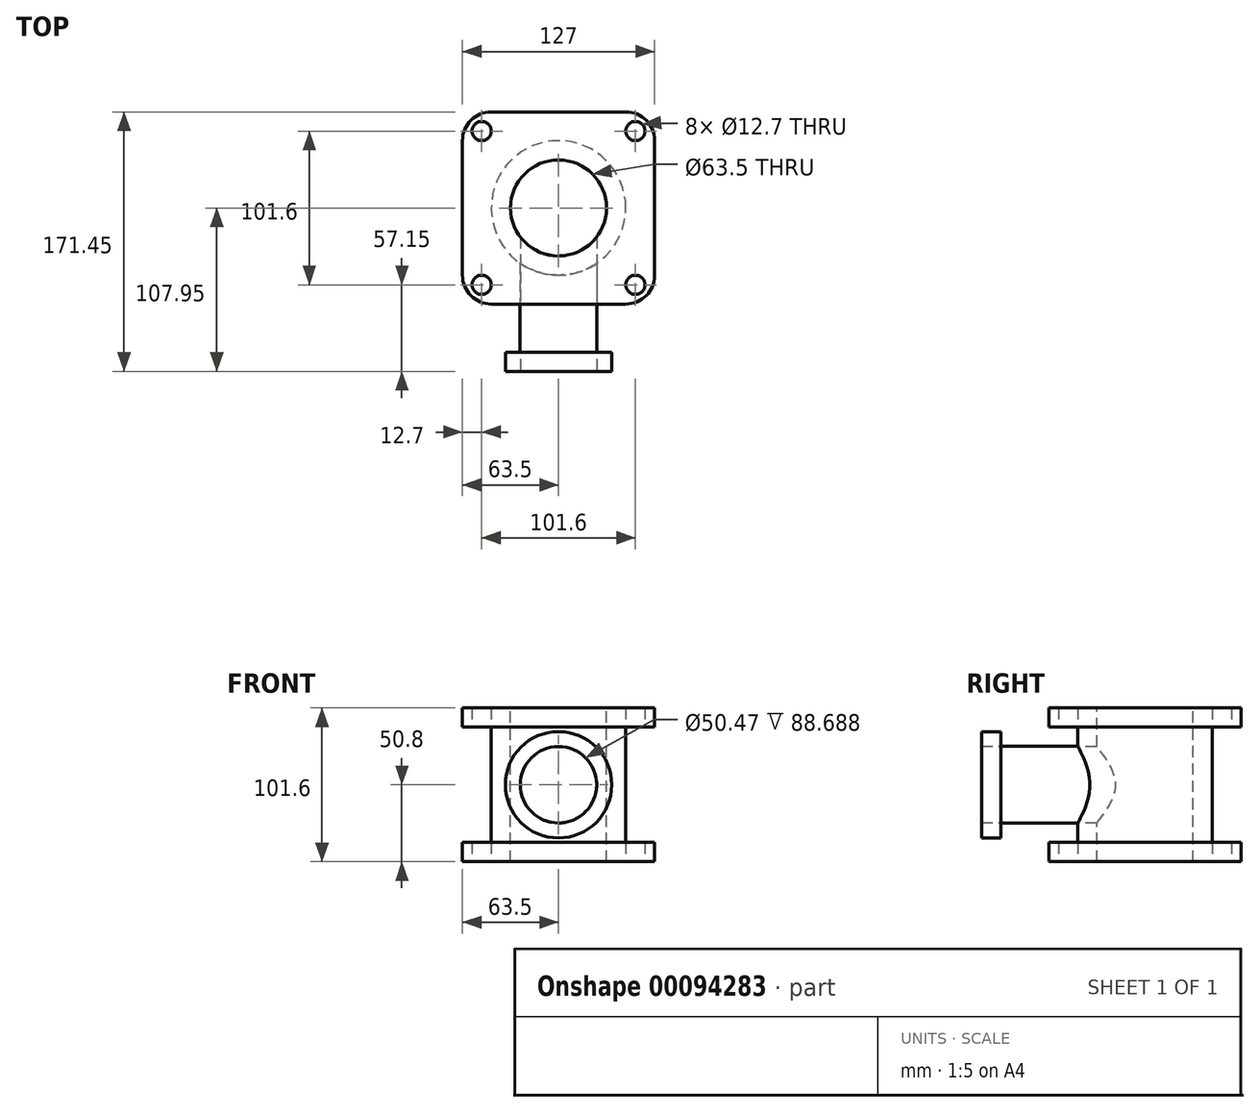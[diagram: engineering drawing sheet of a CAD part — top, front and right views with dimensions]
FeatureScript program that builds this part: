
annotation { "Feature Type Name" : "Feature", "Feature Type Description" : "" }
export const myFeature = defineFeature(function(context is Context, id is Id, definition is map)
    precondition{}
    {
        {
            var Q0;
            Q0=qCreatedBy(makeId("Top.planeOp"),FACE);
            var sketch = newSketch(context, id + "F0", { "sketchPlane" : qUnion([Q0])});
            skLineSegment(sketch, "E0.bottom", {"start": v(63.5, 63.5) * mm, "end": v(-63.5, 63.5) * mm});
            skLineSegment(sketch, "E0.top", {"start": v(63.5, -63.5) * mm, "end": v(-63.5, -63.5) * mm});
            skLineSegment(sketch, "E0.left", {"start": v(63.5, 63.5) * mm, "end": v(63.5, -63.5) * mm});
            skLineSegment(sketch, "E0.right", {"start": v(-63.5, 63.5) * mm, "end": v(-63.5, -63.5) * mm});
            skPoint(sketch, "E0.middle", {"position": v(0, 0) * mm});
            skCircle(sketch, "E1", {"center": v(-50.8, -50.8) * mm, "radius": 6.35 * mm});
            skCircle(sketch, "E2.MirrorC", {"center": v(-50.8, 50.8) * mm, "radius": 6.35 * mm});
            skCircle(sketch, "E3.MirrorC", {"center": v(50.8, 50.8) * mm, "radius": 6.35 * mm});
            skCircle(sketch, "E4.MirrorC", {"center": v(50.8, -50.8) * mm, "radius": 6.35 * mm});
            skSolve(sketch);
        }
        {
            var Q0;
            Q0=makeQuery(id+"F0.imprint","IMPRINT",FACE,{"disambiguationData":[TD([[makeQuery(id+"F0.imprint","IMPRINT",EDGE,{"derivedFrom":sQuery(id+"F0.wireOp",EDGE,"E0.bottom")}),1.0]])]});
            extrude(context, id + "F1", {"entities" : qUnion([Q0]), "depth" : 12.7 * mm});
        }
        {
            var Q0;
            Q0=makeQuery(id+"F1.opExtrude","SWEPT_EDGE",EDGE,{"disambiguationData":[OSD([sQuery(id+"F0.wireOp",EDGE,"E0.bottom"),sQuery(id+"F0.wireOp",EDGE,"E0.right")])]});
            var Q1;
            Q1=makeQuery(id+"F1.opExtrude","SWEPT_EDGE",EDGE,{"disambiguationData":[OSD([sQuery(id+"F0.wireOp",EDGE,"E0.top"),sQuery(id+"F0.wireOp",EDGE,"E0.right")])]});
            var Q2;
            Q2=makeQuery(id+"F1.opExtrude","SWEPT_EDGE",EDGE,{"disambiguationData":[OSD([sQuery(id+"F0.wireOp",EDGE,"E0.bottom"),sQuery(id+"F0.wireOp",EDGE,"E0.left")])]});
            var Q3;
            Q3=makeQuery(id+"F1.opExtrude","SWEPT_EDGE",EDGE,{"disambiguationData":[OSD([sQuery(id+"F0.wireOp",EDGE,"E0.top"),sQuery(id+"F0.wireOp",EDGE,"E0.left")])]});
            fillet(context, id + "F2", {"entities" : qUnion([Q0, Q1, Q2, Q3]), "radius" : 19.05 * mm, "tangentPropagation" : true, "allowEdgeOverflow" : false});
        }
        {
            var Q0;
            Q0=makeQuery(id+"F1.opExtrude","CAP_FACE",FACE,{"disambiguationData":[OSD([sQuery(id+"F0.wireOp",EDGE,"E0.bottom"),sQuery(id+"F0.wireOp",EDGE,"E0.top"),sQuery(id+"F0.wireOp",EDGE,"E0.left"),sQuery(id+"F0.wireOp",EDGE,"E0.right"),sQuery(id+"F0.wireOp",EDGE,"E1"),sQuery(id+"F0.wireOp",EDGE,"E2.MirrorC"),sQuery(id+"F0.wireOp",EDGE,"E3.MirrorC"),sQuery(id+"F0.wireOp",EDGE,"E4.MirrorC")])],"isStart":false});
            var sketch = newSketch(context, id + "F3", { "sketchPlane" : qUnion([Q0])});
            skCircle(sketch, "E5", {"center": v(0, 0) * mm, "radius": 44.45 * mm});
            skSolve(sketch);
        }
        {
            var Q0;
            Q0 = qSketchRegion(id + "F3", true);
            extrude(context, id + "F4", {"entities" : qUnion([Q0]), "operationType" : NewBodyOperationType.ADD, "depth" : 76.2 * mm});
        }
        {
            var Q0;
            Q0=makeQuery(id+"F4.opExtrude","CAP_FACE",FACE,{"disambiguationData":[OSD([sQuery(id+"F3.wireOp",EDGE,"E5")])],"isStart":false});
            var sketch = newSketch(context, id + "F5", { "sketchPlane" : qUnion([Q0])});
            skLineSegment(sketch, "E6.bottom", {"start": v(63.5, 63.5) * mm, "end": v(-63.5, 63.5) * mm});
            skLineSegment(sketch, "E6.top", {"start": v(63.5, -63.5) * mm, "end": v(-63.5, -63.5) * mm});
            skLineSegment(sketch, "E6.left", {"start": v(63.5, 63.5) * mm, "end": v(63.5, -63.5) * mm});
            skLineSegment(sketch, "E6.right", {"start": v(-63.5, 63.5) * mm, "end": v(-63.5, -63.5) * mm});
            skPoint(sketch, "E6.middle", {"position": v(0, 0) * mm});
            skCircle(sketch, "E7", {"center": v(-50.8, 50.8) * mm, "radius": 6.35 * mm});
            skCircle(sketch, "E8.MirrorC", {"center": v(-50.8, -50.8) * mm, "radius": 6.35 * mm});
            skCircle(sketch, "E9.MirrorC", {"center": v(50.8, 50.8) * mm, "radius": 6.35 * mm});
            skCircle(sketch, "E10.MirrorC", {"center": v(50.8, -50.8) * mm, "radius": 6.35 * mm});
            skSolve(sketch);
        }
        {
            var Q0;
            Q0 = qSketchRegion(id + "F5", true);
            extrude(context, id + "F6", {"entities" : qUnion([Q0]), "operationType" : NewBodyOperationType.ADD, "depth" : 12.7 * mm});
        }
        {
            var Q0;
            Q0=makeQuery(id+"F6.opExtrude","SWEPT_EDGE",EDGE,{"disambiguationData":[OSD([sQuery(id+"F5.wireOp",EDGE,"E6.bottom"),sQuery(id+"F5.wireOp",EDGE,"E6.left")])]});
            var Q1;
            Q1=makeQuery(id+"F6.opExtrude","SWEPT_EDGE",EDGE,{"disambiguationData":[OSD([sQuery(id+"F5.wireOp",EDGE,"E6.top"),sQuery(id+"F5.wireOp",EDGE,"E6.left")])]});
            var Q2;
            Q2=makeQuery(id+"F6.opExtrude","SWEPT_EDGE",EDGE,{"disambiguationData":[OSD([sQuery(id+"F5.wireOp",EDGE,"E6.bottom"),sQuery(id+"F5.wireOp",EDGE,"E6.right")])]});
            var Q3;
            Q3=makeQuery(id+"F6.opExtrude","SWEPT_EDGE",EDGE,{"disambiguationData":[OSD([sQuery(id+"F5.wireOp",EDGE,"E6.top"),sQuery(id+"F5.wireOp",EDGE,"E6.right")])]});
            fillet(context, id + "F7", {"entities" : qUnion([Q0, Q1, Q2, Q3]), "radius" : 19.05 * mm, "tangentPropagation" : true, "allowEdgeOverflow" : false});
        }
        {
            var Q0;
            Q0=makeQuery(id+"F6.opExtrude","CAP_FACE",FACE,{"disambiguationData":[OSD([sQuery(id+"F5.wireOp",EDGE,"E6.bottom"),sQuery(id+"F5.wireOp",EDGE,"E6.top"),sQuery(id+"F5.wireOp",EDGE,"E6.left"),sQuery(id+"F5.wireOp",EDGE,"E6.right"),sQuery(id+"F5.wireOp",EDGE,"E7"),sQuery(id+"F5.wireOp",EDGE,"E8.MirrorC"),sQuery(id+"F5.wireOp",EDGE,"E9.MirrorC"),sQuery(id+"F5.wireOp",EDGE,"E10.MirrorC")])],"isStart":false});
            var sketch = newSketch(context, id + "F8", { "sketchPlane" : qUnion([Q0])});
            skCircle(sketch, "E11", {"center": v(0, 0) * mm, "radius": 31.75 * mm});
            skSolve(sketch);
        }
        {
            var Q0;
            Q0 = qSketchRegion(id + "F8", true);
            extrude(context, id + "F9", {"entities" : qUnion([Q0]), "operationType" : NewBodyOperationType.REMOVE, "endBound" : BoundingType.THROUGH_ALL, "oppositeDirection" : true, "depth" : 25.4 * mm});
        }
        {
            var Q0;
            Q0=makeQuery(id+"F6.opExtrude","SWEPT_FACE",FACE,{"disambiguationData":[OSD([sQuery(id+"F5.wireOp",EDGE,"E6.top")])]});
            var sketch = newSketch(context, id + "F10", { "sketchPlane" : qUnion([Q0])});
            skCircle(sketch, "E12", {"center": v(0, 50.8) * mm, "radius": 25.4 * mm});
            skSolve(sketch);
        }
        {
            var Q0;
            Q0=makeQuery(id+"F10.imprint","IMPRINT",FACE,{"disambiguationData":[TD([[makeQuery(id+"F10.imprint","IMPRINT",EDGE,{"derivedFrom":sQuery(id+"F10.wireOp",EDGE,"E12")}),1.0]])]});
            var Q1;
            Q1=makeQuery(id+"F1.opExtrude","SWEPT_BODY",BODY,{"disambiguationData":[OSD([sQuery(id+"F0.wireOp",EDGE,"E0.bottom"),sQuery(id+"F0.wireOp",EDGE,"E0.top"),sQuery(id+"F0.wireOp",EDGE,"E0.left"),sQuery(id+"F0.wireOp",EDGE,"E0.right"),sQuery(id+"F0.wireOp",EDGE,"E1"),sQuery(id+"F0.wireOp",EDGE,"E2.MirrorC"),sQuery(id+"F0.wireOp",EDGE,"E3.MirrorC"),sQuery(id+"F0.wireOp",EDGE,"E4.MirrorC")])]});
            extrude(context, id + "F11", {"entities" : qUnion([Q0]), "operationType" : NewBodyOperationType.ADD, "endBound" : BoundingType.SYMMETRIC, "oppositeDirection" : true, "endBoundEntityBody" : qUnion([Q1]), "depth" : 63.5 * mm});
        }
        {
            var Q0;
            Q0=makeQuery(id+"F11.opExtrude","CAP_FACE",FACE,{"disambiguationData":[OSD([sQuery(id+"F10.wireOp",EDGE,"E12")])],"isStart":true});
            var sketch = newSketch(context, id + "F12", { "sketchPlane" : qUnion([Q0])});
            skCircle(sketch, "E13", {"center": v(0, 50.8) * mm, "radius": 35.16 * mm});
            skSolve(sketch);
        }
        {
            var Q0;
            Q0 = qSketchRegion(id + "F12", true);
            extrude(context, id + "F13", {"entities" : qUnion([Q0]), "operationType" : NewBodyOperationType.ADD, "depth" : 12.7 * mm});
        }
        {
            var Q0;
            Q0=makeQuery(id+"F13.opExtrude","CAP_FACE",FACE,{"disambiguationData":[OSD([sQuery(id+"F12.wireOp",EDGE,"E13")])],"isStart":false});
            var sketch = newSketch(context, id + "F14", { "sketchPlane" : qUnion([Q0])});
            skCircle(sketch, "E14", {"center": v(0, 50.8) * mm, "radius": 25.23 * mm});
            skSolve(sketch);
        }
        {
            var Q0;
            Q0 = qSketchRegion(id + "F14", true);
            var Q1;
            Q1=makeQuery(id+"F4.opExtrude","SWEPT_FACE",FACE,{"disambiguationData":[OSD([sQuery(id+"F3.wireOp",EDGE,"E5")])]});
            var Q2;
            Q2=makeQuery(id+"F1.opExtrude","SWEPT_BODY",BODY,{"disambiguationData":[OSD([sQuery(id+"F0.wireOp",EDGE,"E0.bottom"),sQuery(id+"F0.wireOp",EDGE,"E0.top"),sQuery(id+"F0.wireOp",EDGE,"E0.left"),sQuery(id+"F0.wireOp",EDGE,"E0.right"),sQuery(id+"F0.wireOp",EDGE,"E1"),sQuery(id+"F0.wireOp",EDGE,"E2.MirrorC"),sQuery(id+"F0.wireOp",EDGE,"E3.MirrorC"),sQuery(id+"F0.wireOp",EDGE,"E4.MirrorC")])]});
            extrude(context, id + "F15", {"entities" : qUnion([Q0]), "operationType" : NewBodyOperationType.REMOVE, "endBound" : BoundingType.UP_TO_BODY, "oppositeDirection" : true, "endBoundEntityFace" : qUnion([Q1]), "endBoundEntityBody" : qUnion([Q2]), "depth" : 25.4 * mm});
        }
    });
